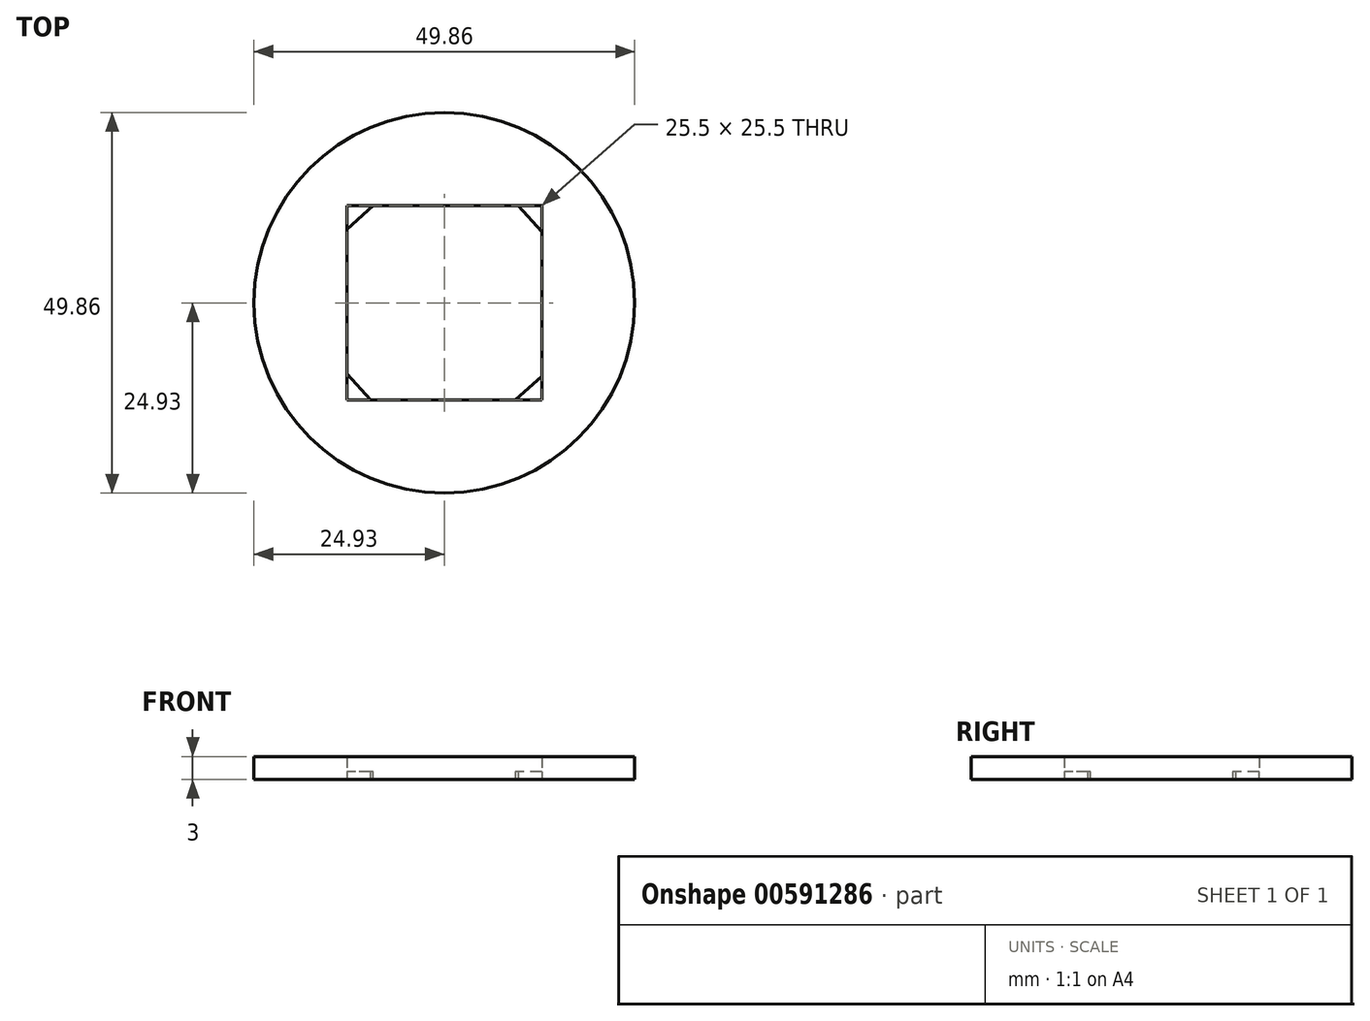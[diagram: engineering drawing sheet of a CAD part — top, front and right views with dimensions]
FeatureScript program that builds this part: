
annotation { "Feature Type Name" : "Feature", "Feature Type Description" : "" }
export const myFeature = defineFeature(function(context is Context, id is Id, definition is map)
    precondition{}
    {
        {
            var Q0;
            Q0=qCreatedBy(makeId("Top.planeOp"),FACE);
            var sketch = newSketch(context, id + "F0", { "sketchPlane" : qUnion([Q0])});
            skLineSegment(sketch, "E0.bottom", {"start": v(12.75, 12.75) * mm, "end": v(-12.75, 12.75) * mm});
            skLineSegment(sketch, "E0.top", {"start": v(12.75, -12.75) * mm, "end": v(-12.75, -12.75) * mm});
            skLineSegment(sketch, "E0.left", {"start": v(12.75, 12.75) * mm, "end": v(12.75, -12.75) * mm});
            skLineSegment(sketch, "E0.right", {"start": v(-12.75, 12.75) * mm, "end": v(-12.75, -12.75) * mm});
            skPoint(sketch, "E0.middle", {"position": v(0, 0) * mm});
            skCircle(sketch, "E1", {"center": v(0, 0) * mm, "radius": 24.93 * mm});
            skSolve(sketch);
        }
        {
            var Q0;
            Q0 = qSketchRegion(id + "F0", true);
            extrude(context, id + "F1", {"entities" : qUnion([Q0]), "depth" : 3 * mm, "offsetDistance" : 25 * mm});
        }
        {
            var Q0;
            Q0=qCreatedBy(makeId("Top.planeOp"),FACE);
            var sketch = newSketch(context, id + "F2", { "sketchPlane" : qUnion([Q0])});
            skLineSegment(sketch, "E2", {"start": v(-13.92, -8.01) * mm, "end": v(-8.36, -14.17) * mm});
            skLineSegment(sketch, "E3", {"start": v(-14.61, -14.57) * mm, "end": v(-13.92, -8.01) * mm});
            skLineSegment(sketch, "E4", {"start": v(-14.61, -14.57) * mm, "end": v(-8.36, -14.17) * mm});
            skLineSegment(sketch, "E5.1.0", {"start": v(8.01, -13.92) * mm, "end": v(14.17, -8.36) * mm});
            skLineSegment(sketch, "E5.1.1", {"start": v(14.57, -14.61) * mm, "end": v(8.01, -13.92) * mm});
            skLineSegment(sketch, "E5.1.2", {"start": v(14.57, -14.61) * mm, "end": v(14.17, -8.36) * mm});
            skLineSegment(sketch, "E5.2.0", {"start": v(13.92, 8.01) * mm, "end": v(8.36, 14.17) * mm});
            skLineSegment(sketch, "E5.2.1", {"start": v(14.61, 14.57) * mm, "end": v(13.92, 8.01) * mm});
            skLineSegment(sketch, "E5.2.2", {"start": v(14.61, 14.57) * mm, "end": v(8.36, 14.17) * mm});
            skLineSegment(sketch, "E5.3.0", {"start": v(-8.01, 13.92) * mm, "end": v(-14.17, 8.36) * mm});
            skLineSegment(sketch, "E5.3.1", {"start": v(-14.57, 14.61) * mm, "end": v(-8.01, 13.92) * mm});
            skLineSegment(sketch, "E5.3.2", {"start": v(-14.57, 14.61) * mm, "end": v(-14.17, 8.36) * mm});
            skPoint(sketch, "E5.center", {"position": v(0, 0) * mm});
            skSolve(sketch);
        }
        {
            var Q0;
            Q0 = qSketchRegion(id + "F2", true);
            extrude(context, id + "F3", {"entities" : qUnion([Q0]), "operationType" : NewBodyOperationType.ADD, "depth" : 1 * mm, "offsetDistance" : 25 * mm});
        }
    });
